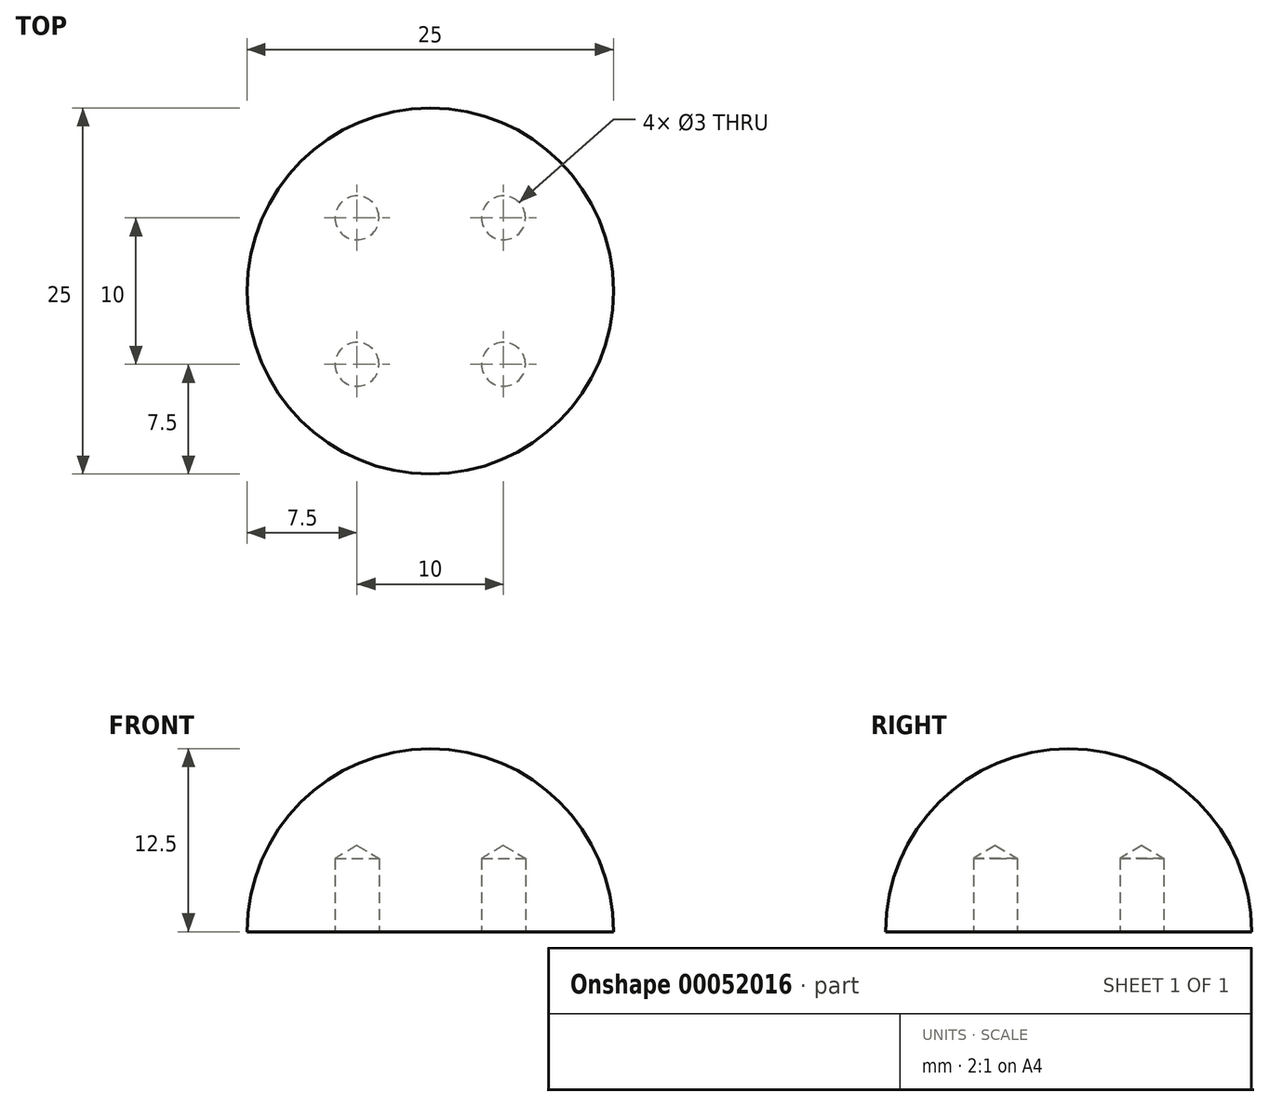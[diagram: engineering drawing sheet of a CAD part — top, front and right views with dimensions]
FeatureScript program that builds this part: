
annotation { "Feature Type Name" : "Feature", "Feature Type Description" : "" }
export const myFeature = defineFeature(function(context is Context, id is Id, definition is map)
    precondition{}
    {
        {
            var Q0;
            Q0=qCreatedBy(makeId("Top.planeOp"),FACE);
            var sketch = newSketch(context, id + "F0", { "sketchPlane" : qUnion([Q0])});
            skCircle(sketch, "E0", {"center": v(0, 0) * mm, "radius": 12.5 * mm});
            skLineSegment(sketch, "E1", {"start": v(-12.5, 0) * mm, "end": v(12.5, 0) * mm});
            skSolve(sketch);
        }
        {
            var Q0;
            {var subQ0=sQuery(id+"F0.wireOp",EDGE,"E1");Q0=makeQuery(id+"F0.imprint","IMPRINT",FACE,{"disambiguationData":[TD([[makeQuery(id+"F0.imprint","IMPRINT",EDGE,{"derivedFrom":subQ0}),1.0]])]});}
            var Q1;
            Q1=sQuery(id+"F0.wireOp",EDGE,"E1");
            revolve(context, id + "F1", {"entities" : qUnion([Q0]), "axis" : qUnion([Q1]), "revolveType" : RevolveType.ONE_DIRECTION, "angle" : 180 * degree});
        }
        {
            var Q0;
            Q0=makeQuery(id+"F1.opRevolve","CAP_FACE",FACE,{"disambiguationData":[OSD([sQuery(id+"F0.wireOp",EDGE,"E0"),sQuery(id+"F0.wireOp",EDGE,"E1")])],"isStart":true});
            var sketch = newSketch(context, id + "F2", { "sketchPlane" : qUnion([Q0])});
            skLineSegment(sketch, "E2.bottom", {"start": v(-5, 5) * mm, "end": v(5, 5) * mm});
            skLineSegment(sketch, "E2.top", {"start": v(-5, -5) * mm, "end": v(5, -5) * mm});
            skLineSegment(sketch, "E2.left", {"start": v(-5, 5) * mm, "end": v(-5, -5) * mm});
            skLineSegment(sketch, "E2.right", {"start": v(5, 5) * mm, "end": v(5, -5) * mm});
            skLineSegment(sketch, "E3", {"start": v(-5, 5) * mm, "end": v(5, -5) * mm});
            skPoint(sketch, "E4", {"position": v(0, 0) * mm});
            skSolve(sketch);
        }
        {
            var Q0;
            Q0=sQuery(id+"F2.wireOp",VERTEX,"E2.left.start");
            var Q1;
            Q1=sQuery(id+"F2.wireOp",VERTEX,"E2.bottom.end");
            var Q2;
            Q2=sQuery(id+"F2.wireOp",VERTEX,"E2.top.end");
            var Q3;
            Q3=sQuery(id+"F2.wireOp",VERTEX,"E2.left.end");
            var Q4;
            Q4=makeQuery(id+"F1.opRevolve","SWEPT_BODY",BODY,{"disambiguationData":[OSD([sQuery(id+"F0.wireOp",EDGE,"E0"),sQuery(id+"F0.wireOp",EDGE,"E1")])]});
            hole(context, id + "F3", {"style" : HoleStyle.SIMPLE, "endStyle" : HoleEndStyle.BLIND, "holeDiameter" : 3 * mm, "holeDepth" : 5 * mm, "locations" : qUnion([Q0, Q1, Q2, Q3]), "scope" : qUnion([Q4])});
        }
    });
